# Revit family: Sink-Undermount-Kitchen-KALLISTA-Soltiere-L20307
name_source: partatom
category: Plumbing Fixtures
units: mm (PartAtom-declared; Revit-internal decimal feet)

## family parameters
Cut with Voids When Loaded = No
Host = Face
Maintain Annotation Orientation = No
OmniClass Number = 23.31.13.00
Part Type = Normal
Room Calculation Point = No
Round Connector Dimension = Use Diameter
Shared = No

## types (1)
- NA-Stainless Steel
    ADA Compliant = No
    Assembly Code = D2010400
    CW Connection = No
    Cold Water Inlet = Cold Water Inlet
    Date Modified = 05/14/2025
    Default Elevation = 36"
    Description = 45 Inch Stainless Steel Kitchen Sink with Standard Accessories
    Drain Included = No
    Finish = Kallista-Metal-NA-Stainless_Steel
    HW Connection = No
    Height = 13 1/2"
    Hot Water Inlet = Hot Water Inlet
    Length = 45"
    Manufacturer = Kallista Co.
    Master Format 2014 = 22 41 16
    Master Format 2014 Name = Residential Lavatories and Sinks
    Material = Stainless Steel
    Model = L20307-00-NA
    Product Documentation Link = https://techcomm.kohler.com
    Product Name = Multiere
    Product Page URL = https://www.kallista.com
    Type = 1
    URL = https://www.kallista.com
    Vent Connection = No
    Waste Connection = Yes
    Waste Water Outlet = Waste Water Outlet
    WaterSense Certified = No
    Width = 18"

## geometry (parser evidence)
native form markers: Sweep x8
no freeform markers — native parametric forms only
